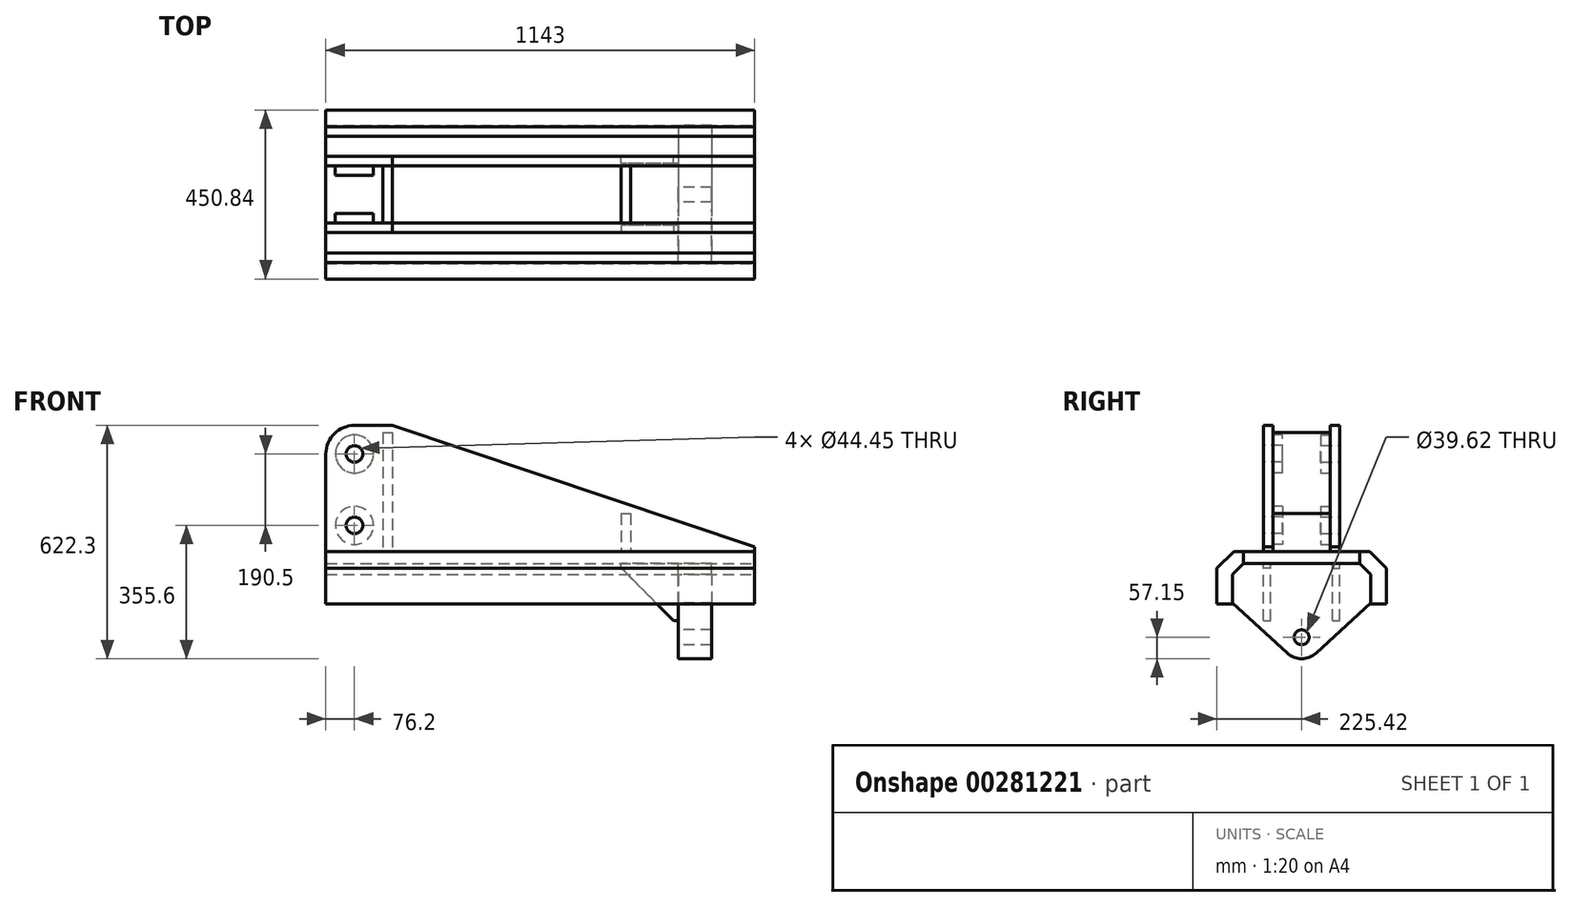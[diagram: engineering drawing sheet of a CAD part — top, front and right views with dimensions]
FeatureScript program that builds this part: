
annotation { "Feature Type Name" : "Feature", "Feature Type Description" : "" }
export const myFeature = defineFeature(function(context is Context, id is Id, definition is map)
    precondition{}
    {
        {
            var Q0;
            Q0=qCreatedBy(makeId("Top.planeOp"),FACE);
            var sketch = newSketch(context, id + "F0", { "sketchPlane" : qUnion([Q0])});
            skLineSegment(sketch, "E0.bottom", {"start": v(-571.5, 155.58) * mm, "end": v(571.5, 155.58) * mm});
            skLineSegment(sketch, "E0.top", {"start": v(-571.5, -155.58) * mm, "end": v(571.5, -155.58) * mm});
            skLineSegment(sketch, "E0.left", {"start": v(-571.5, 155.58) * mm, "end": v(-571.5, -155.58) * mm});
            skLineSegment(sketch, "E0.right", {"start": v(571.5, 155.58) * mm, "end": v(571.5, -155.58) * mm});
            skPoint(sketch, "E0.middle", {"position": v(0, 0) * mm});
            skSolve(sketch);
        }
        {
            var Q0;
            Q0 = qSketchRegion(id + "F0", true);
            extrude(context, id + "F1", {"entities" : qUnion([Q0]), "depth" : 31.75 * mm});
        }
        {
            var Q0;
            Q0=makeQuery(id+"F1.opExtrude","CAP_FACE",FACE,{"disambiguationData":[OSD([sQuery(id+"F0.wireOp",EDGE,"E0.bottom"),sQuery(id+"F0.wireOp",EDGE,"E0.top"),sQuery(id+"F0.wireOp",EDGE,"E0.left"),sQuery(id+"F0.wireOp",EDGE,"E0.right")])],"isStart":false});
            var sketch = newSketch(context, id + "F2", { "sketchPlane" : qUnion([Q0])});
            skLineSegment(sketch, "E1", {"start": v(-735.89, 0) * mm, "end": v(703.14, 0) * mm, "construction": true});
            skLineSegment(sketch, "E2.0", {"start": v(-419.1, 76.2) * mm, "end": v(-419.1, -76.2) * mm});
            skLineSegment(sketch, "E3.0", {"start": v(-393.7, 76.2) * mm, "end": v(-393.7, -76.2) * mm});
            skLineSegment(sketch, "E4.0", {"start": v(-419.1, -76.2) * mm, "end": v(-393.7, -76.2) * mm});
            skLineSegment(sketch, "E5.MirrorCS", {"start": v(-419.1, 76.2) * mm, "end": v(-393.7, 76.2) * mm});
            skSolve(sketch);
        }
        {
            var Q0;
            Q0 = qSketchRegion(id + "F2", true);
            extrude(context, id + "F3", {"entities" : qUnion([Q0]), "operationType" : NewBodyOperationType.ADD, "depth" : 317.5 * mm});
        }
        {
            var Q0;
            Q0=makeQuery(id+"F1.opExtrude","CAP_FACE",FACE,{"disambiguationData":[OSD([sQuery(id+"F0.wireOp",EDGE,"E0.bottom"),sQuery(id+"F0.wireOp",EDGE,"E0.top"),sQuery(id+"F0.wireOp",EDGE,"E0.left"),sQuery(id+"F0.wireOp",EDGE,"E0.right")])],"isStart":false});
            var sketch = newSketch(context, id + "F4", { "sketchPlane" : qUnion([Q0])});
            skLineSegment(sketch, "E6.0", {"start": v(215.9, 76.2) * mm, "end": v(215.9, -76.2) * mm});
            skLineSegment(sketch, "E7.0", {"start": v(241.3, 76.2) * mm, "end": v(241.3, -76.2) * mm});
            skLineSegment(sketch, "E8.0", {"start": v(-419.1, 76.2) * mm, "end": v(-419.1, -76.2) * mm, "construction": true});
            skLineSegment(sketch, "E9", {"start": v(215.9, 76.2) * mm, "end": v(241.3, 76.2) * mm});
            skLineSegment(sketch, "E10", {"start": v(215.9, -76.2) * mm, "end": v(241.3, -76.2) * mm});
            skSolve(sketch);
        }
        {
            var Q0;
            Q0 = qSketchRegion(id + "F4", true);
            extrude(context, id + "F5", {"entities" : qUnion([Q0]), "operationType" : NewBodyOperationType.ADD, "depth" : 101.6 * mm});
        }
        {
            var Q0;
            Q0=makeQuery(id+"F3.opExtrude","SWEPT_FACE",FACE,{"disambiguationData":[OSD([sQuery(id+"F2.wireOp",EDGE,"E4.0")])]});
            var sketch = newSketch(context, id + "F6", { "sketchPlane" : qUnion([Q0])});
            skLineSegment(sketch, "E11.0", {"start": v(-571.5, 31.75) * mm, "end": v(571.5, 31.75) * mm});
            skLineSegment(sketch, "E12.0", {"start": v(-495.3, 368.3) * mm, "end": v(-393.7, 368.3) * mm});
            skLineSegment(sketch, "E13", {"start": v(-571.5, 292.1) * mm, "end": v(-571.5, 31.75) * mm});
            skLineSegment(sketch, "E14.0", {"start": v(-571.5, 44.45) * mm, "end": v(571.5, 44.45) * mm, "construction": true});
            skLineSegment(sketch, "E15.0", {"start": v(-393.7, 368.3) * mm, "end": v(-393.7, 31.75) * mm, "construction": true});
            skPoint(sketch, "E16.orphan", {"position": v(-393.7, 349.25) * mm});
            skLineSegment(sketch, "E17", {"start": v(-393.7, 368.3) * mm, "end": v(571.5, 44.45) * mm});
            skLineSegment(sketch, "E18", {"start": v(571.5, 31.75) * mm, "end": v(571.5, 44.45) * mm});
            skPoint(sketch, "E19.visualSharp", {"position": v(-571.5, 368.3) * mm});
            skArc(sketch, "E19.filletArc", {"start": v(-495.3, 368.3) * mm, "mid": v(-549.18, 345.98) * mm, "end": v(-571.5, 292.1) * mm});
            skSolve(sketch);
        }
        {
            var Q0;
            Q0 = qSketchRegion(id + "F6", true);
            extrude(context, id + "F7", {"entities" : qUnion([Q0]), "depth" : 25.4 * mm});
        }
        {
            var Q0;
            Q0=makeQuery(id+"F7.opExtrude","CAP_FACE",FACE,{"disambiguationData":[OSD([sQuery(id+"F6.wireOp",EDGE,"E11.0"),sQuery(id+"F6.wireOp",EDGE,"E12.0"),sQuery(id+"F6.wireOp",EDGE,"E13"),sQuery(id+"F6.wireOp",EDGE,"E17"),sQuery(id+"F6.wireOp",EDGE,"E18"),sQuery(id+"F6.wireOp",EDGE,"E19.filletArc")])],"isStart":false});
            var sketch = newSketch(context, id + "F8", { "sketchPlane" : qUnion([Q0])});
            skArc(sketch, "E20.0", {"start": v(-495.3, 368.3) * mm, "mid": v(-549.18, 345.98) * mm, "end": v(-571.5, 292.1) * mm, "construction": true});
            skLineSegment(sketch, "E21", {"start": v(-495.3, 292.1) * mm, "end": v(-495.3, 101.6) * mm, "construction": true});
            skPoint(sketch, "E22", {"position": v(-495.3, 101.6) * mm});
            skSolve(sketch);
        }
        {
            var Q0;
            Q0=sQuery(id+"F8.wireOp",VERTEX,"E20.0.center");
            var Q1;
            Q1=sQuery(id+"F8.wireOp",VERTEX,"E22");
            var Q2;
            Q2=makeQuery(id+"F7.opExtrude","SWEPT_BODY",BODY,{"disambiguationData":[OSD([sQuery(id+"F6.wireOp",EDGE,"E11.0"),sQuery(id+"F6.wireOp",EDGE,"E12.0"),sQuery(id+"F6.wireOp",EDGE,"E13"),sQuery(id+"F6.wireOp",EDGE,"E17"),sQuery(id+"F6.wireOp",EDGE,"E18"),sQuery(id+"F6.wireOp",EDGE,"E19.filletArc")])]});
            hole(context, id + "F9", {"style" : HoleStyle.SIMPLE, "endStyle" : HoleEndStyle.THROUGH, "holeDiameter" : 44.45 * mm, "tappedDepth" : 42.34 * mm, "tapClearance" : 3, "startFromSketch" : true, "locations" : qUnion([Q0, Q1]), "scope" : qUnion([Q2])});
        }
        {
            var Q0;
            Q0=makeQuery(id+"F7.opExtrude","CAP_FACE",FACE,{"disambiguationData":[OSD([sQuery(id+"F6.wireOp",EDGE,"E11.0"),sQuery(id+"F6.wireOp",EDGE,"E12.0"),sQuery(id+"F6.wireOp",EDGE,"E13"),sQuery(id+"F6.wireOp",EDGE,"E17"),sQuery(id+"F6.wireOp",EDGE,"E18"),sQuery(id+"F6.wireOp",EDGE,"E19.filletArc")])],"isStart":true});
            var sketch = newSketch(context, id + "F10", { "sketchPlane" : qUnion([Q0])});
            skCircle(sketch, "E23.0", {"center": v(495.3, 101.6) * mm, "radius": 22.22 * mm});
            skCircle(sketch, "E24.0", {"center": v(495.3, 292.1) * mm, "radius": 22.22 * mm});
            skCircle(sketch, "E25", {"center": v(495.3, 101.6) * mm, "radius": 50.8 * mm});
            skCircle(sketch, "E26", {"center": v(495.3, 292.1) * mm, "radius": 50.8 * mm});
            skSolve(sketch);
        }
        {
            var Q0;
            Q0 = qSketchRegion(id + "F10", true);
            extrude(context, id + "F11", {"entities" : qUnion([Q0]), "operationType" : NewBodyOperationType.ADD, "depth" : 25.4 * mm});
        }
        {
            var Q0;
            Q0=makeQuery(id+"F7.opExtrude","SWEPT_BODY",BODY,{"disambiguationData":[OSD([sQuery(id+"F6.wireOp",EDGE,"E11.0"),sQuery(id+"F6.wireOp",EDGE,"E12.0"),sQuery(id+"F6.wireOp",EDGE,"E13"),sQuery(id+"F6.wireOp",EDGE,"E17"),sQuery(id+"F6.wireOp",EDGE,"E18"),sQuery(id+"F6.wireOp",EDGE,"E19.filletArc")])]});
            var Q1;
            Q1=qCreatedBy(makeId("Front.planeOp"),FACE);
            mirror(context, id + "F12", {"entities" : qUnion([Q0]), "mirrorPlane" : qUnion([Q1])});
        }
        {
            var Q0;
            Q0=makeQuery(id+"F1.opExtrude","SWEPT_FACE",FACE,{"disambiguationData":[OSD([sQuery(id+"F0.wireOp",EDGE,"E0.left")])]});
            cPlane(context, id + "F13", {"entities" : qUnion([Q0]), "cplaneType" : CPlaneType.OFFSET, "offset" : 939.8 * mm, "oppositeDirection" : true, "width" : 152.4 * mm, "height" : 152.4 * mm});
        }
        {
            var Q0;
            Q0=qCreatedBy(id+"F13.planeOp",FACE);
            var sketch = newSketch(context, id + "F14", { "sketchPlane" : qUnion([Q0])});
            skLineSegment(sketch, "E27", {"start": v(0, 471.48) * mm, "end": v(0, -357.9) * mm, "construction": true});
            skLineSegment(sketch, "E28.0", {"start": v(-155.57, 0) * mm, "end": v(155.58, 0) * mm});
            skLineSegment(sketch, "E29.0", {"start": v(-155.57, -254) * mm, "end": v(155.58, -254) * mm});
            skLineSegment(sketch, "E30.0", {"start": v(-155.57, -196.85) * mm, "end": v(155.58, -196.85) * mm, "construction": true});
            skArc(sketch, "E31", {"start": v(-38.72, -238.88) * mm, "mid": v(0, -254) * mm, "end": v(38.72, -238.88) * mm});
            skLineSegment(sketch, "E32.0", {"start": v(-184.15, -104.9) * mm, "end": v(155.58, -104.9) * mm, "construction": true});
            skLineSegment(sketch, "E33.0", {"start": v(-184.15, 471.48) * mm, "end": v(-184.15, -357.9) * mm, "construction": true});
            skLineSegment(sketch, "E34.0", {"start": v(-184.15, -28.7) * mm, "end": v(155.58, -28.7) * mm, "construction": true});
            skLineSegment(sketch, "E35", {"start": v(-184.15, -28.7) * mm, "end": v(-184.15, -104.9) * mm});
            skLineSegment(sketch, "E36", {"start": v(-184.15, -104.9) * mm, "end": v(-38.72, -238.88) * mm});
            skLineSegment(sketch, "E37", {"start": v(-184.15, -28.7) * mm, "end": v(-155.57, 0) * mm});
            skLineSegment(sketch, "E38.MirrorCS", {"start": v(184.15, -104.9) * mm, "end": v(38.72, -238.88) * mm});
            skLineSegment(sketch, "E39.MirrorCS", {"start": v(184.15, -28.7) * mm, "end": v(155.57, 0) * mm});
            skLineSegment(sketch, "E40.MirrorCS", {"start": v(184.15, -28.7) * mm, "end": v(184.15, -104.9) * mm});
            skCircle(sketch, "E41", {"center": v(0, -196.85) * mm, "radius": 19.81 * mm});
            skSolve(sketch);
        }
        {
            var Q0;
            Q0 = qSketchRegion(id + "F14", true);
            extrude(context, id + "F15", {"entities" : qUnion([Q0]), "oppositeDirection" : true, "depth" : 88.9 * mm});
        }
        {
            var Q0;
            Q0=makeQuery(id+"F1.opExtrude","CAP_FACE",FACE,{"disambiguationData":[OSD([sQuery(id+"F0.wireOp",EDGE,"E0.bottom"),sQuery(id+"F0.wireOp",EDGE,"E0.top"),sQuery(id+"F0.wireOp",EDGE,"E0.left"),sQuery(id+"F0.wireOp",EDGE,"E0.right")])],"isStart":true});
            var sketch = newSketch(context, id + "F16", { "sketchPlane" : qUnion([Q0])});
            skLineSegment(sketch, "E42.0", {"start": v(-571.5, -76.2) * mm, "end": v(571.5, -76.2) * mm, "construction": true});
            skLineSegment(sketch, "E43.0", {"start": v(368.3, -184.15) * mm, "end": v(368.3, -38.72) * mm, "construction": true});
            skLineSegment(sketch, "E44.0", {"start": v(-571.5, -101.6) * mm, "end": v(571.5, -101.6) * mm, "construction": true});
            skLineSegment(sketch, "E45.bottom", {"start": v(368.3, -101.6) * mm, "end": v(215.9, -101.6) * mm});
            skLineSegment(sketch, "E45.top", {"start": v(368.3, -82.55) * mm, "end": v(215.9, -82.55) * mm});
            skLineSegment(sketch, "E45.left", {"start": v(368.3, -101.6) * mm, "end": v(368.3, -82.55) * mm});
            skLineSegment(sketch, "E45.right", {"start": v(215.9, -101.6) * mm, "end": v(215.9, -82.55) * mm});
            skSolve(sketch);
        }
        {
            var Q0;
            Q0 = qSketchRegion(id + "F16", true);
            extrude(context, id + "F17", {"entities" : qUnion([Q0]), "depth" : 152.4 * mm});
        }
        {
            var Q0;
            Q0=makeQuery(id+"F17.opExtrude","SWEPT_FACE",FACE,{"disambiguationData":[OSD([sQuery(id+"F16.wireOp",EDGE,"E45.bottom")])]});
            var sketch = newSketch(context, id + "F18", { "sketchPlane" : qUnion([Q0])});
            skLineSegment(sketch, "E46.0", {"start": v(571.5, -12.7) * mm, "end": v(-571.5, -12.7) * mm, "construction": true});
            skLineSegment(sketch, "E47.0", {"start": v(-355.6, -251.58) * mm, "end": v(-355.6, -92.2) * mm, "construction": true});
            skLineSegment(sketch, "E47.1", {"start": v(-469.9, -251.58) * mm, "end": v(-355.6, -251.58) * mm, "construction": true});
            skLineSegment(sketch, "E47.2", {"start": v(-469.9, -92.2) * mm, "end": v(-469.9, -251.58) * mm, "construction": true});
            skLineSegment(sketch, "E47.3", {"start": v(-355.6, -92.2) * mm, "end": v(-469.9, -92.2) * mm, "construction": true});
            skLineSegment(sketch, "E48", {"start": v(-355.6, -152.4) * mm, "end": v(-215.9, -12.7) * mm});
            skPoint(sketch, "E48.startSnap0", {"position": v(-292.1, -152.4) * mm});
            skLineSegment(sketch, "E49", {"start": v(-215.9, -12.7) * mm, "end": v(-215.9, -152.4) * mm});
            skLineSegment(sketch, "E50", {"start": v(-215.9, -152.4) * mm, "end": v(-355.6, -152.4) * mm});
            skSolve(sketch);
        }
        {
            var Q0;
            Q0 = qSketchRegion(id + "F18", true);
            extrude(context, id + "F19", {"entities" : qUnion([Q0]), "operationType" : NewBodyOperationType.REMOVE, "endBound" : BoundingType.THROUGH_ALL, "oppositeDirection" : true, "depth" : 25.4 * mm});
        }
        {
            var Q0;
            Q0=makeQuery(id+"F17.opExtrude","SWEPT_BODY",BODY,{"disambiguationData":[OSD([sQuery(id+"F16.wireOp",EDGE,"E45.bottom"),sQuery(id+"F16.wireOp",EDGE,"E45.top"),sQuery(id+"F16.wireOp",EDGE,"E45.left"),sQuery(id+"F16.wireOp",EDGE,"E45.right")])]});
            var Q1;
            Q1=qCreatedBy(makeId("Front.planeOp"),FACE);
            mirror(context, id + "F20", {"entities" : qUnion([Q0]), "mirrorPlane" : qUnion([Q1])});
        }
        {
            var Q0;
            Q0=makeQuery(id+"F1.opExtrude","SWEPT_FACE",FACE,{"disambiguationData":[OSD([sQuery(id+"F0.wireOp",EDGE,"E0.right")])]});
            var sketch = newSketch(context, id + "F21", { "sketchPlane" : qUnion([Q0])});
            skLineSegment(sketch, "E51.0", {"start": v(155.58, 31.75) * mm, "end": v(155.58, 0) * mm});
            skLineSegment(sketch, "E52.0", {"start": v(184.15, -28.7) * mm, "end": v(155.57, 0) * mm});
            skLineSegment(sketch, "E53.0", {"start": v(225.43, 31.75) * mm, "end": v(225.43, 0) * mm});
            skLineSegment(sketch, "E54", {"start": v(155.58, 31.75) * mm, "end": v(180.98, 31.75) * mm});
            skLineSegment(sketch, "E55", {"start": v(180.98, 31.75) * mm, "end": v(225.43, -12.7) * mm});
            skLineSegment(sketch, "E56", {"start": v(225.43, -12.7) * mm, "end": v(225.43, -107.95) * mm});
            skLineSegment(sketch, "E57.0", {"start": v(191.38, -107.95) * mm, "end": v(225.43, -107.95) * mm});
            skLineSegment(sketch, "E58", {"start": v(184.15, -28.7) * mm, "end": v(184.15, -107.95) * mm});
            skLineSegment(sketch, "E59", {"start": v(184.15, -107.95) * mm, "end": v(191.38, -107.95) * mm});
            skSolve(sketch);
        }
        {
            var Q0;
            Q0 = qSketchRegion(id + "F21", true);
            extrude(context, id + "F22", {"entities" : qUnion([Q0]), "oppositeDirection" : true, "depth" : 1143 * mm});
        }
        {
            var Q0;
            Q0=makeQuery(id+"F22.opExtrude","SWEPT_BODY",BODY,{"disambiguationData":[OSD([sQuery(id+"F21.wireOp",EDGE,"E51.0"),sQuery(id+"F21.wireOp",EDGE,"E52.0"),sQuery(id+"F21.wireOp",EDGE,"E54"),sQuery(id+"F21.wireOp",EDGE,"E55"),sQuery(id+"F21.wireOp",EDGE,"E56"),sQuery(id+"F21.wireOp",EDGE,"E57.0"),sQuery(id+"F21.wireOp",EDGE,"E58"),sQuery(id+"F21.wireOp",EDGE,"E59")])]});
            var Q1;
            Q1=qCreatedBy(makeId("Front.planeOp"),FACE);
            mirror(context, id + "F23", {"entities" : qUnion([Q0]), "mirrorPlane" : qUnion([Q1])});
        }
    });
